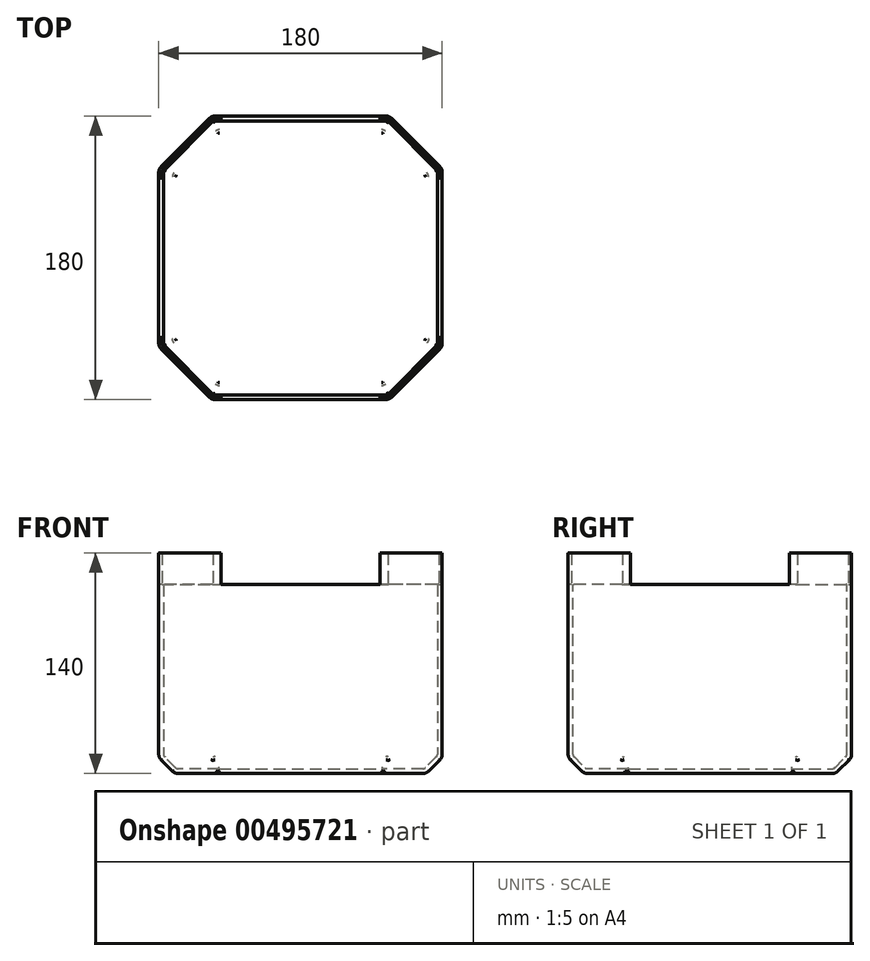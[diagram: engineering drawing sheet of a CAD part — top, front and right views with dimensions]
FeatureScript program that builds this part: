
annotation { "Feature Type Name" : "Feature", "Feature Type Description" : "" }
export const myFeature = defineFeature(function(context is Context, id is Id, definition is map)
    precondition{}
    {
        {
            var Q0;
            Q0=qCreatedBy(makeId("Top.planeOp"),FACE);
            var sketch = newSketch(context, id + "F0", { "sketchPlane" : qUnion([Q0])});
            skLineSegment(sketch, "E0.bottom", {"start": v(-56.5, 90) * mm, "end": v(56.5, 90) * mm});
            skLineSegment(sketch, "E0.top", {"start": v(-56.5, -90) * mm, "end": v(56.5, -90) * mm});
            skLineSegment(sketch, "E0.left", {"start": v(-90, 56.5) * mm, "end": v(-90, -56.5) * mm});
            skLineSegment(sketch, "E0.right", {"start": v(90, 56.5) * mm, "end": v(90, -56.5) * mm});
            skLineSegment(sketch, "E1", {"start": v(0, 156.9) * mm, "end": v(0, -146.72) * mm, "construction": true});
            skLineSegment(sketch, "E2", {"start": v(-149.43, 0) * mm, "end": v(169.81, 0) * mm, "construction": true});
            skLineSegment(sketch, "E3", {"start": v(-90, 56.5) * mm, "end": v(-56.5, 90) * mm});
            skLineSegment(sketch, "E4", {"start": v(-90, -56.5) * mm, "end": v(-56.5, -90) * mm});
            skLineSegment(sketch, "E5", {"start": v(56.5, -90) * mm, "end": v(90, -56.5) * mm});
            skLineSegment(sketch, "E6", {"start": v(56.5, 90) * mm, "end": v(90, 56.5) * mm});
            skPoint(sketch, "E7.orphan", {"position": v(-90, 90) * mm});
            skPoint(sketch, "E8.orphan", {"position": v(90, 90) * mm});
            skPoint(sketch, "E9.orphan", {"position": v(90, -90) * mm});
            skPoint(sketch, "E10.orphan", {"position": v(-90, -90) * mm});
            skSolve(sketch);
        }
        {
            var Q0;
            Q0=qSketchRegion(id+"F0",true);
            extrude(context, id + "F1", {"entities" : qUnion([Q0]), "depth" : 120 * mm});
        }
        {
            var Q0;
            Q0=makeQuery(id+"F1.opExtrude","CAP_EDGE",EDGE,{"disambiguationData":[OSD([sQuery(id+"F0.wireOp",EDGE,"E0.top")])],"isStart":true});
            var Q1;
            Q1=makeQuery(id+"F1.opExtrude","CAP_EDGE",EDGE,{"disambiguationData":[OSD([sQuery(id+"F0.wireOp",EDGE,"E4")])],"isStart":true});
            var Q2;
            Q2=makeQuery(id+"F1.opExtrude","CAP_EDGE",EDGE,{"disambiguationData":[OSD([sQuery(id+"F0.wireOp",EDGE,"E0.left")])],"isStart":true});
            var Q3;
            Q3=makeQuery(id+"F1.opExtrude","CAP_EDGE",EDGE,{"disambiguationData":[OSD([sQuery(id+"F0.wireOp",EDGE,"E3")])],"isStart":true});
            var Q4;
            Q4=makeQuery(id+"F1.opExtrude","CAP_EDGE",EDGE,{"disambiguationData":[OSD([sQuery(id+"F0.wireOp",EDGE,"E0.bottom")])],"isStart":true});
            var Q5;
            Q5=makeQuery(id+"F1.opExtrude","CAP_EDGE",EDGE,{"disambiguationData":[OSD([sQuery(id+"F0.wireOp",EDGE,"E6")])],"isStart":true});
            var Q6;
            Q6=makeQuery(id+"F1.opExtrude","CAP_EDGE",EDGE,{"disambiguationData":[OSD([sQuery(id+"F0.wireOp",EDGE,"E0.right")])],"isStart":true});
            var Q7;
            Q7=makeQuery(id+"F1.opExtrude","CAP_EDGE",EDGE,{"disambiguationData":[OSD([sQuery(id+"F0.wireOp",EDGE,"E5")])],"isStart":true});
            chamfer(context, id + "F2", {"entities" : qUnion([Q0, Q1, Q2, Q3, Q4, Q5, Q6, Q7]), "chamferType" : ChamferType.TWO_OFFSETS, "width1" : 10 * mm, "oppositeDirection" : true, "width2" : 10 * mm, "tangentPropagation" : true});
        }
        {
            var Q0;
            Q0=makeQuery(id+"F1.opExtrude","CAP_FACE",FACE,{"disambiguationData":[OSD([sQuery(id+"F0.wireOp",EDGE,"E0.bottom"),sQuery(id+"F0.wireOp",EDGE,"E0.top"),sQuery(id+"F0.wireOp",EDGE,"E0.left"),sQuery(id+"F0.wireOp",EDGE,"E0.right"),sQuery(id+"F0.wireOp",EDGE,"E3"),sQuery(id+"F0.wireOp",EDGE,"E4"),sQuery(id+"F0.wireOp",EDGE,"E5"),sQuery(id+"F0.wireOp",EDGE,"E6")])],"isStart":false});
            var sketch = newSketch(context, id + "F3", { "sketchPlane" : qUnion([Q0])});
            skLineSegment(sketch, "E11", {"start": v(90, -56.5) * mm, "end": v(56.5, -90) * mm});
            skLineSegment(sketch, "E12.0", {"start": v(88, -55.67) * mm, "end": v(55.67, -88) * mm});
            skLineSegment(sketch, "E13", {"start": v(90, -56.5) * mm, "end": v(90, -90) * mm, "construction": true});
            skLineSegment(sketch, "E14", {"start": v(90, -90) * mm, "end": v(56.5, -90) * mm, "construction": true});
            skLineSegment(sketch, "E15", {"start": v(90, -56.5) * mm, "end": v(90, -50.5) * mm});
            skLineSegment(sketch, "E16", {"start": v(56.5, -90) * mm, "end": v(50.5, -90) * mm});
            skLineSegment(sketch, "E17.0", {"start": v(55.67, -88) * mm, "end": v(50.5, -88) * mm});
            skLineSegment(sketch, "E18.0", {"start": v(88, -55.67) * mm, "end": v(88, -50.5) * mm});
            skLineSegment(sketch, "E19", {"start": v(88, -50.5) * mm, "end": v(90, -50.5) * mm});
            skLineSegment(sketch, "E20", {"start": v(50.5, -88) * mm, "end": v(50.5, -90) * mm});
            skLineSegment(sketch, "E21", {"start": v(104.54, 0) * mm, "end": v(-130.04, 0) * mm, "construction": true});
            skPoint(sketch, "E21.endSnap0", {"position": v(-90, 0) * mm});
            skLineSegment(sketch, "E22", {"start": v(0, 121.87) * mm, "end": v(0, -139.26) * mm, "construction": true});
            skLineSegment(sketch, "E23.MirrorCS", {"start": v(88, 50.5) * mm, "end": v(90, 50.5) * mm});
            skLineSegment(sketch, "E24.MirrorCS", {"start": v(50.5, 88) * mm, "end": v(50.5, 90) * mm});
            skLineSegment(sketch, "E25.MirrorCS", {"start": v(56.5, 90) * mm, "end": v(50.5, 90) * mm});
            skLineSegment(sketch, "E26.MirrorCS", {"start": v(55.67, 88) * mm, "end": v(50.5, 88) * mm});
            skLineSegment(sketch, "E27.MirrorCS", {"start": v(88, 55.67) * mm, "end": v(88, 50.5) * mm});
            skLineSegment(sketch, "E28.MirrorCS", {"start": v(90, 56.5) * mm, "end": v(90, 50.5) * mm});
            skLineSegment(sketch, "E29.MirrorCS", {"start": v(90, 56.5) * mm, "end": v(56.5, 90) * mm});
            skLineSegment(sketch, "E30.MirrorCS", {"start": v(88, 55.67) * mm, "end": v(55.67, 88) * mm});
            skLineSegment(sketch, "E31.MirrorCS", {"start": v(90, 90) * mm, "end": v(56.5, 90) * mm, "construction": true});
            skLineSegment(sketch, "E32.MirrorCS", {"start": v(90, 56.5) * mm, "end": v(90, 90) * mm, "construction": true});
            skLineSegment(sketch, "E33.MirrorCS", {"start": v(-88, 50.5) * mm, "end": v(-90, 50.5) * mm});
            skLineSegment(sketch, "E34.MirrorCS", {"start": v(-50.5, 88) * mm, "end": v(-50.5, 90) * mm});
            skLineSegment(sketch, "E35.MirrorCS", {"start": v(-88, -50.5) * mm, "end": v(-90, -50.5) * mm});
            skLineSegment(sketch, "E36.MirrorCS", {"start": v(-50.5, -88) * mm, "end": v(-50.5, -90) * mm});
            skLineSegment(sketch, "E37.MirrorCS", {"start": v(-56.5, -90) * mm, "end": v(-50.5, -90) * mm});
            skLineSegment(sketch, "E38.MirrorCS", {"start": v(-88, 55.67) * mm, "end": v(-88, 50.5) * mm});
            skLineSegment(sketch, "E39.MirrorCS", {"start": v(-56.5, 90) * mm, "end": v(-50.5, 90) * mm});
            skLineSegment(sketch, "E40.MirrorCS", {"start": v(-88, 55.67) * mm, "end": v(-55.67, 88) * mm});
            skLineSegment(sketch, "E41.MirrorCS", {"start": v(-88, -55.67) * mm, "end": v(-88, -50.5) * mm});
            skLineSegment(sketch, "E42.MirrorCS", {"start": v(-90, 56.5) * mm, "end": v(-56.5, 90) * mm});
            skLineSegment(sketch, "E43.MirrorCS", {"start": v(-55.67, 88) * mm, "end": v(-50.5, 88) * mm});
            skLineSegment(sketch, "E44.MirrorCS", {"start": v(-90, 56.5) * mm, "end": v(-90, 50.5) * mm});
            skLineSegment(sketch, "E45.MirrorCS", {"start": v(-90, -56.5) * mm, "end": v(-90, -50.5) * mm});
            skLineSegment(sketch, "E46.MirrorCS", {"start": v(-55.67, -88) * mm, "end": v(-50.5, -88) * mm});
            skLineSegment(sketch, "E47.MirrorCS", {"start": v(-90, 90) * mm, "end": v(-56.5, 90) * mm, "construction": true});
            skLineSegment(sketch, "E48.MirrorCS", {"start": v(-90, 56.5) * mm, "end": v(-90, 90) * mm, "construction": true});
            skLineSegment(sketch, "E49.MirrorCS", {"start": v(-90, -56.5) * mm, "end": v(-56.5, -90) * mm});
            skLineSegment(sketch, "E50.MirrorCS", {"start": v(-90, -56.5) * mm, "end": v(-90, -90) * mm, "construction": true});
            skLineSegment(sketch, "E51.MirrorCS", {"start": v(-90, -90) * mm, "end": v(-56.5, -90) * mm, "construction": true});
            skLineSegment(sketch, "E52.MirrorCS", {"start": v(-88, -55.67) * mm, "end": v(-55.67, -88) * mm});
            skSolve(sketch);
        }
        {
            var Q0;
            Q0=qSketchRegion(id+"F3",true);
            extrude(context, id + "F4", {"entities" : qUnion([Q0]), "operationType" : NewBodyOperationType.ADD, "depth" : 20 * mm});
        }
        {
            var Q0;
            {var subQ0=sQuery(id+"F0.wireOp",EDGE,"E6");Q0=makeQuery(id+"F2.opChamfer","BLEND_EDGE",EDGE,{"blendedFrom":[makeQuery(id+"F1.opExtrude","CAP_EDGE",EDGE,{"disambiguationData":[OSD([subQ0])],"isStart":true}),makeQuery(id+"F1.opExtrude","SWEPT_FACE",FACE,{"disambiguationData":[OSD([subQ0])]})],"blendedInto":[makeQuery(id+"F1.opExtrude","SWEPT_FACE",FACE,{"disambiguationData":[OSD([subQ0])]})]});}
            var Q1;
            {var subQ0=sQuery(id+"F0.wireOp",EDGE,"E0.right");Q1=makeQuery(id+"F2.opChamfer","BLEND_EDGE",EDGE,{"blendedFrom":[makeQuery(id+"F1.opExtrude","CAP_EDGE",EDGE,{"disambiguationData":[OSD([subQ0])],"isStart":true}),makeQuery(id+"F1.opExtrude","SWEPT_FACE",FACE,{"disambiguationData":[OSD([subQ0])]})],"blendedInto":[makeQuery(id+"F1.opExtrude","SWEPT_FACE",FACE,{"disambiguationData":[OSD([subQ0])]})]});}
            var Q2;
            {var subQ0=sQuery(id+"F0.wireOp",EDGE,"E5");Q2=makeQuery(id+"F2.opChamfer","BLEND_EDGE",EDGE,{"blendedFrom":[makeQuery(id+"F1.opExtrude","CAP_EDGE",EDGE,{"disambiguationData":[OSD([subQ0])],"isStart":true}),makeQuery(id+"F1.opExtrude","SWEPT_FACE",FACE,{"disambiguationData":[OSD([subQ0])]})],"blendedInto":[makeQuery(id+"F1.opExtrude","SWEPT_FACE",FACE,{"disambiguationData":[OSD([subQ0])]})]});}
            var Q3;
            {var subQ0=sQuery(id+"F0.wireOp",EDGE,"E0.top");Q3=makeQuery(id+"F2.opChamfer","BLEND_EDGE",EDGE,{"blendedFrom":[makeQuery(id+"F1.opExtrude","CAP_EDGE",EDGE,{"disambiguationData":[OSD([subQ0])],"isStart":true}),makeQuery(id+"F1.opExtrude","SWEPT_FACE",FACE,{"disambiguationData":[OSD([subQ0])]})],"blendedInto":[makeQuery(id+"F1.opExtrude","SWEPT_FACE",FACE,{"disambiguationData":[OSD([subQ0])]})]});}
            var Q4;
            {var subQ0=sQuery(id+"F0.wireOp",EDGE,"E4");Q4=makeQuery(id+"F2.opChamfer","BLEND_EDGE",EDGE,{"blendedFrom":[makeQuery(id+"F1.opExtrude","CAP_EDGE",EDGE,{"disambiguationData":[OSD([subQ0])],"isStart":true}),makeQuery(id+"F1.opExtrude","SWEPT_FACE",FACE,{"disambiguationData":[OSD([subQ0])]})],"blendedInto":[makeQuery(id+"F1.opExtrude","SWEPT_FACE",FACE,{"disambiguationData":[OSD([subQ0])]})]});}
            var Q5;
            {var subQ0=sQuery(id+"F0.wireOp",EDGE,"E0.left");Q5=makeQuery(id+"F2.opChamfer","BLEND_EDGE",EDGE,{"blendedFrom":[makeQuery(id+"F1.opExtrude","CAP_EDGE",EDGE,{"disambiguationData":[OSD([subQ0])],"isStart":true}),makeQuery(id+"F1.opExtrude","SWEPT_FACE",FACE,{"disambiguationData":[OSD([subQ0])]})],"blendedInto":[makeQuery(id+"F1.opExtrude","SWEPT_FACE",FACE,{"disambiguationData":[OSD([subQ0])]})]});}
            var Q6;
            {var subQ0=sQuery(id+"F0.wireOp",EDGE,"E3");Q6=makeQuery(id+"F2.opChamfer","BLEND_EDGE",EDGE,{"blendedFrom":[makeQuery(id+"F1.opExtrude","CAP_EDGE",EDGE,{"disambiguationData":[OSD([subQ0])],"isStart":true}),makeQuery(id+"F1.opExtrude","SWEPT_FACE",FACE,{"disambiguationData":[OSD([subQ0])]})],"blendedInto":[makeQuery(id+"F1.opExtrude","SWEPT_FACE",FACE,{"disambiguationData":[OSD([subQ0])]})]});}
            var Q7;
            {var subQ0=sQuery(id+"F0.wireOp",EDGE,"E0.bottom");Q7=makeQuery(id+"F2.opChamfer","BLEND_EDGE",EDGE,{"blendedFrom":[makeQuery(id+"F1.opExtrude","CAP_EDGE",EDGE,{"disambiguationData":[OSD([subQ0])],"isStart":true}),makeQuery(id+"F1.opExtrude","SWEPT_FACE",FACE,{"disambiguationData":[OSD([subQ0])]})],"blendedInto":[makeQuery(id+"F1.opExtrude","SWEPT_FACE",FACE,{"disambiguationData":[OSD([subQ0])]})]});}
            fillet(context, id + "F5", {"entities" : qUnion([Q0, Q1, Q2, Q3, Q4, Q5, Q6, Q7]), "radius" : 5 * mm, "tangentPropagation" : true, "allowEdgeOverflow" : false});
        }
        {
            var Q0;
            Q0=makeQuery(id+"F4.boolean.opBoolean","MERGE",EDGE,{"derivedFrom":[makeQuery(id+"F1.opExtrude","SWEPT_EDGE",EDGE,{"disambiguationData":[OSD([sQuery(id+"F0.wireOp",EDGE,"E0.bottom"),sQuery(id+"F0.wireOp",EDGE,"E6")])]}),makeQuery(id+"F4.opExtrude","SWEPT_EDGE",EDGE,{"disambiguationData":[OSD([sQuery(id+"F3.wireOp",EDGE,"E25.MirrorCS"),sQuery(id+"F3.wireOp",EDGE,"E29.MirrorCS")])]})]});
            var Q1;
            Q1=makeQuery(id+"F4.boolean.opBoolean","MERGE",EDGE,{"derivedFrom":[makeQuery(id+"F1.opExtrude","SWEPT_EDGE",EDGE,{"disambiguationData":[OSD([sQuery(id+"F0.wireOp",EDGE,"E0.right"),sQuery(id+"F0.wireOp",EDGE,"E6")])]}),makeQuery(id+"F4.opExtrude","SWEPT_EDGE",EDGE,{"disambiguationData":[OSD([sQuery(id+"F3.wireOp",EDGE,"E28.MirrorCS"),sQuery(id+"F3.wireOp",EDGE,"E29.MirrorCS")])]})]});
            var Q2;
            Q2=makeQuery(id+"F4.boolean.opBoolean","MERGE",EDGE,{"derivedFrom":[makeQuery(id+"F1.opExtrude","SWEPT_EDGE",EDGE,{"disambiguationData":[OSD([sQuery(id+"F0.wireOp",EDGE,"E0.bottom"),sQuery(id+"F0.wireOp",EDGE,"E3")])]}),makeQuery(id+"F4.opExtrude","SWEPT_EDGE",EDGE,{"disambiguationData":[OSD([sQuery(id+"F3.wireOp",EDGE,"E39.MirrorCS"),sQuery(id+"F3.wireOp",EDGE,"E42.MirrorCS")])]})]});
            var Q3;
            Q3=makeQuery(id+"F4.boolean.opBoolean","MERGE",EDGE,{"derivedFrom":[makeQuery(id+"F1.opExtrude","SWEPT_EDGE",EDGE,{"disambiguationData":[OSD([sQuery(id+"F0.wireOp",EDGE,"E0.right"),sQuery(id+"F0.wireOp",EDGE,"E5")])]}),makeQuery(id+"F4.opExtrude","SWEPT_EDGE",EDGE,{"disambiguationData":[OSD([sQuery(id+"F3.wireOp",EDGE,"E11"),sQuery(id+"F3.wireOp",EDGE,"E15")])]})]});
            var Q4;
            Q4=makeQuery(id+"F2.opChamfer","BLEND_EDGE",EDGE,{"blendedFrom":[makeQuery(id+"F1.opExtrude","CAP_EDGE",EDGE,{"disambiguationData":[OSD([sQuery(id+"F0.wireOp",EDGE,"E0.top")])],"isStart":true}),makeQuery(id+"F1.opExtrude","CAP_EDGE",EDGE,{"disambiguationData":[OSD([sQuery(id+"F0.wireOp",EDGE,"E5")])],"isStart":true})],"blendedInto":[]});
            var Q5;
            Q5=makeQuery(id+"F2.opChamfer","BLEND_EDGE",EDGE,{"blendedFrom":[makeQuery(id+"F1.opExtrude","CAP_EDGE",EDGE,{"disambiguationData":[OSD([sQuery(id+"F0.wireOp",EDGE,"E0.top")])],"isStart":true}),makeQuery(id+"F1.opExtrude","CAP_EDGE",EDGE,{"disambiguationData":[OSD([sQuery(id+"F0.wireOp",EDGE,"E4")])],"isStart":true})],"blendedInto":[]});
            var Q6;
            Q6=makeQuery(id+"F2.opChamfer","BLEND_EDGE",EDGE,{"blendedFrom":[makeQuery(id+"F1.opExtrude","CAP_EDGE",EDGE,{"disambiguationData":[OSD([sQuery(id+"F0.wireOp",EDGE,"E0.left")])],"isStart":true}),makeQuery(id+"F1.opExtrude","CAP_EDGE",EDGE,{"disambiguationData":[OSD([sQuery(id+"F0.wireOp",EDGE,"E4")])],"isStart":true})],"blendedInto":[]});
            var Q7;
            Q7=makeQuery(id+"F2.opChamfer","BLEND_EDGE",EDGE,{"blendedFrom":[makeQuery(id+"F1.opExtrude","CAP_EDGE",EDGE,{"disambiguationData":[OSD([sQuery(id+"F0.wireOp",EDGE,"E0.left")])],"isStart":true}),makeQuery(id+"F1.opExtrude","CAP_EDGE",EDGE,{"disambiguationData":[OSD([sQuery(id+"F0.wireOp",EDGE,"E3")])],"isStart":true})],"blendedInto":[]});
            fillet(context, id + "F6", {"entities" : qUnion([Q0, Q1, Q2, Q3, Q4, Q5, Q6, Q7]), "radius" : 5 * mm, "tangentPropagation" : true, "allowEdgeOverflow" : false});
        }
        {
            var Q0;
            {var subQ0=sQuery(id+"F0.wireOp",EDGE,"E0.left");Q0=makeQuery(id+"F2.opChamfer","BLEND_EDGE",EDGE,{"blendedFrom":[makeQuery(id+"F1.opExtrude","CAP_EDGE",EDGE,{"disambiguationData":[OSD([subQ0])],"isStart":true}),makeQuery(id+"F1.opExtrude","CAP_FACE",FACE,{"disambiguationData":[OSD([sQuery(id+"F0.wireOp",EDGE,"E0.bottom"),sQuery(id+"F0.wireOp",EDGE,"E0.top"),subQ0,sQuery(id+"F0.wireOp",EDGE,"E0.right"),sQuery(id+"F0.wireOp",EDGE,"E3"),sQuery(id+"F0.wireOp",EDGE,"E4"),sQuery(id+"F0.wireOp",EDGE,"E5"),sQuery(id+"F0.wireOp",EDGE,"E6")])],"isStart":true})],"blendedInto":[makeQuery(id+"F1.opExtrude","CAP_FACE",FACE,{"disambiguationData":[OSD([sQuery(id+"F0.wireOp",EDGE,"E0.bottom"),sQuery(id+"F0.wireOp",EDGE,"E0.top"),subQ0,sQuery(id+"F0.wireOp",EDGE,"E0.right"),sQuery(id+"F0.wireOp",EDGE,"E3"),sQuery(id+"F0.wireOp",EDGE,"E4"),sQuery(id+"F0.wireOp",EDGE,"E5"),sQuery(id+"F0.wireOp",EDGE,"E6")])],"isStart":true})]});}
            fillet(context, id + "F7", {"entities" : qUnion([Q0]), "radius" : 5 * mm, "tangentPropagation" : true, "allowEdgeOverflow" : false});
        }
        {
            var Q0;
            Q0=makeQuery(id+"F1.opExtrude","CAP_FACE",FACE,{"disambiguationData":[OSD([sQuery(id+"F0.wireOp",EDGE,"E0.bottom"),sQuery(id+"F0.wireOp",EDGE,"E0.top"),sQuery(id+"F0.wireOp",EDGE,"E0.left"),sQuery(id+"F0.wireOp",EDGE,"E0.right"),sQuery(id+"F0.wireOp",EDGE,"E3"),sQuery(id+"F0.wireOp",EDGE,"E4"),sQuery(id+"F0.wireOp",EDGE,"E5"),sQuery(id+"F0.wireOp",EDGE,"E6")])],"isStart":false});
            shell(context, id + "F8", {"entities" : qUnion([Q0]), "thickness" : 3 * mm});
        }
    });
